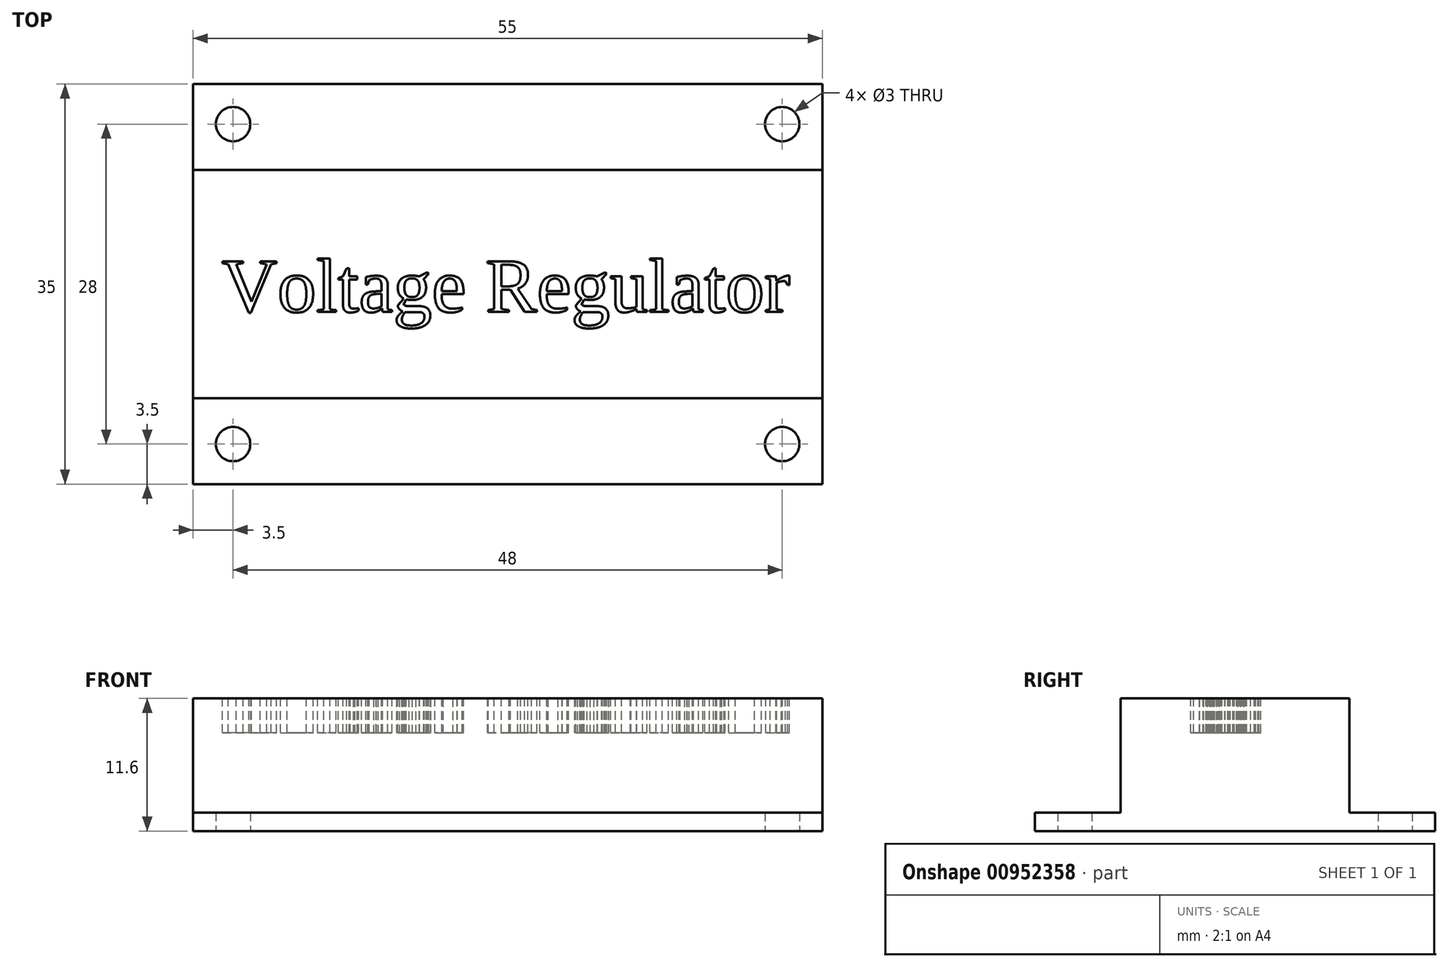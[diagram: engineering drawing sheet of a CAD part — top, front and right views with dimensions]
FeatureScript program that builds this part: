
annotation { "Feature Type Name" : "Feature", "Feature Type Description" : "" }
export const myFeature = defineFeature(function(context is Context, id is Id, definition is map)
    precondition{}
    {
        {
            var Q0;
            Q0=qCreatedBy(makeId("Top.planeOp"),FACE);
            var sketch = newSketch(context, id + "F0", { "sketchPlane" : qUnion([Q0])});
            skLineSegment(sketch, "E0.bottom", {"start": v(27.5, 17.5) * mm, "end": v(-27.5, 17.5) * mm});
            skLineSegment(sketch, "E0.top", {"start": v(27.5, -17.5) * mm, "end": v(-27.5, -17.5) * mm});
            skLineSegment(sketch, "E0.left", {"start": v(27.5, 17.5) * mm, "end": v(27.5, -17.5) * mm});
            skLineSegment(sketch, "E0.right", {"start": v(-27.5, 17.5) * mm, "end": v(-27.5, -17.5) * mm});
            skPoint(sketch, "E0.middle", {"position": v(0, 0) * mm});
            skCircle(sketch, "E1", {"center": v(-24, 14) * mm, "radius": 1.5 * mm});
            skCircle(sketch, "E2.0.1.0", {"center": v(-24, -14) * mm, "radius": 1.5 * mm});
            skCircle(sketch, "E2.1.0.0", {"center": v(24, 14) * mm, "radius": 1.5 * mm});
            skCircle(sketch, "E2.1.1.0", {"center": v(24, -14) * mm, "radius": 1.5 * mm});
            skLineSegment(sketch, "E2.direction1", {"start": v(-24, 14) * mm, "end": v(24, 14) * mm, "construction": true});
            skLineSegment(sketch, "E2.direction2", {"start": v(-24, 14) * mm, "end": v(-24, -14) * mm, "construction": true});
            skPoint(sketch, "E3.positionSnap0", {"position": v(-24, 0) * mm});
            skPoint(sketch, "E4", {"position": v(0, 14) * mm});
            skSolve(sketch);
        }
        {
            var Q0;
            Q0 = qSketchRegion(id + "F0", true);
            extrude(context, id + "F1", {"entities" : qUnion([Q0]), "depth" : 1.6 * mm, "offsetDistance" : 25 * mm});
        }
        {
            var Q0;
            Q0=makeQuery(id+"F1.opExtrude","CAP_FACE",FACE,{"disambiguationData":[OSD([sQuery(id+"F0.wireOp",EDGE,"E0.bottom"),sQuery(id+"F0.wireOp",EDGE,"E0.top"),sQuery(id+"F0.wireOp",EDGE,"E0.left"),sQuery(id+"F0.wireOp",EDGE,"E0.right"),sQuery(id+"F0.wireOp",EDGE,"E1"),sQuery(id+"F0.wireOp",EDGE,"E2.0.1.0"),sQuery(id+"F0.wireOp",EDGE,"E2.1.0.0"),sQuery(id+"F0.wireOp",EDGE,"E2.1.1.0")])],"isStart":false});
            var sketch = newSketch(context, id + "F2", { "sketchPlane" : qUnion([Q0])});
            skLineSegment(sketch, "E5.bottom", {"start": v(27.5, 10) * mm, "end": v(-27.5, 10) * mm});
            skLineSegment(sketch, "E5.top", {"start": v(27.5, -10) * mm, "end": v(-27.5, -10) * mm});
            skLineSegment(sketch, "E5.left", {"start": v(27.5, 10) * mm, "end": v(27.5, -10) * mm});
            skLineSegment(sketch, "E5.right", {"start": v(-27.5, 10) * mm, "end": v(-27.5, -10) * mm});
            skPoint(sketch, "E5.middle", {"position": v(0, 0) * mm});
            skSolve(sketch);
        }
        {
            var Q0;
            Q0 = qSketchRegion(id + "F2", true);
            extrude(context, id + "F3", {"entities" : qUnion([Q0]), "operationType" : NewBodyOperationType.ADD, "depth" : 10 * mm, "offsetDistance" : 25 * mm});
        }
        {
            var Q0;
            Q0=makeQuery(id+"F3.opExtrude","CAP_FACE",FACE,{"disambiguationData":[OSD([sQuery(id+"F2.wireOp",EDGE,"E5.bottom"),sQuery(id+"F2.wireOp",EDGE,"E5.top"),sQuery(id+"F2.wireOp",EDGE,"E5.left"),sQuery(id+"F2.wireOp",EDGE,"E5.right")])],"isStart":false});
            var sketch = newSketch(context, id + "F4", { "sketchPlane" : qUnion([Q0])});
            skText(sketch, "E6", { "text": "Voltage Regulator", "fontName": "Tinos-Regular.ttf"});
            const initialGuessF4  = {"E6": [-0.025, -0.00243, 1, 0, 0.00486]};
            skSetInitialGuess(sketch, initialGuessF4);
            skSolve(sketch);
        }
        {
            var Q0;
            Q0 = qSketchRegion(id + "F4", true);
            extrude(context, id + "F5", {"entities" : qUnion([Q0]), "operationType" : NewBodyOperationType.REMOVE, "oppositeDirection" : true, "depth" : 3 * mm, "offsetDistance" : 25 * mm});
        }
    });
